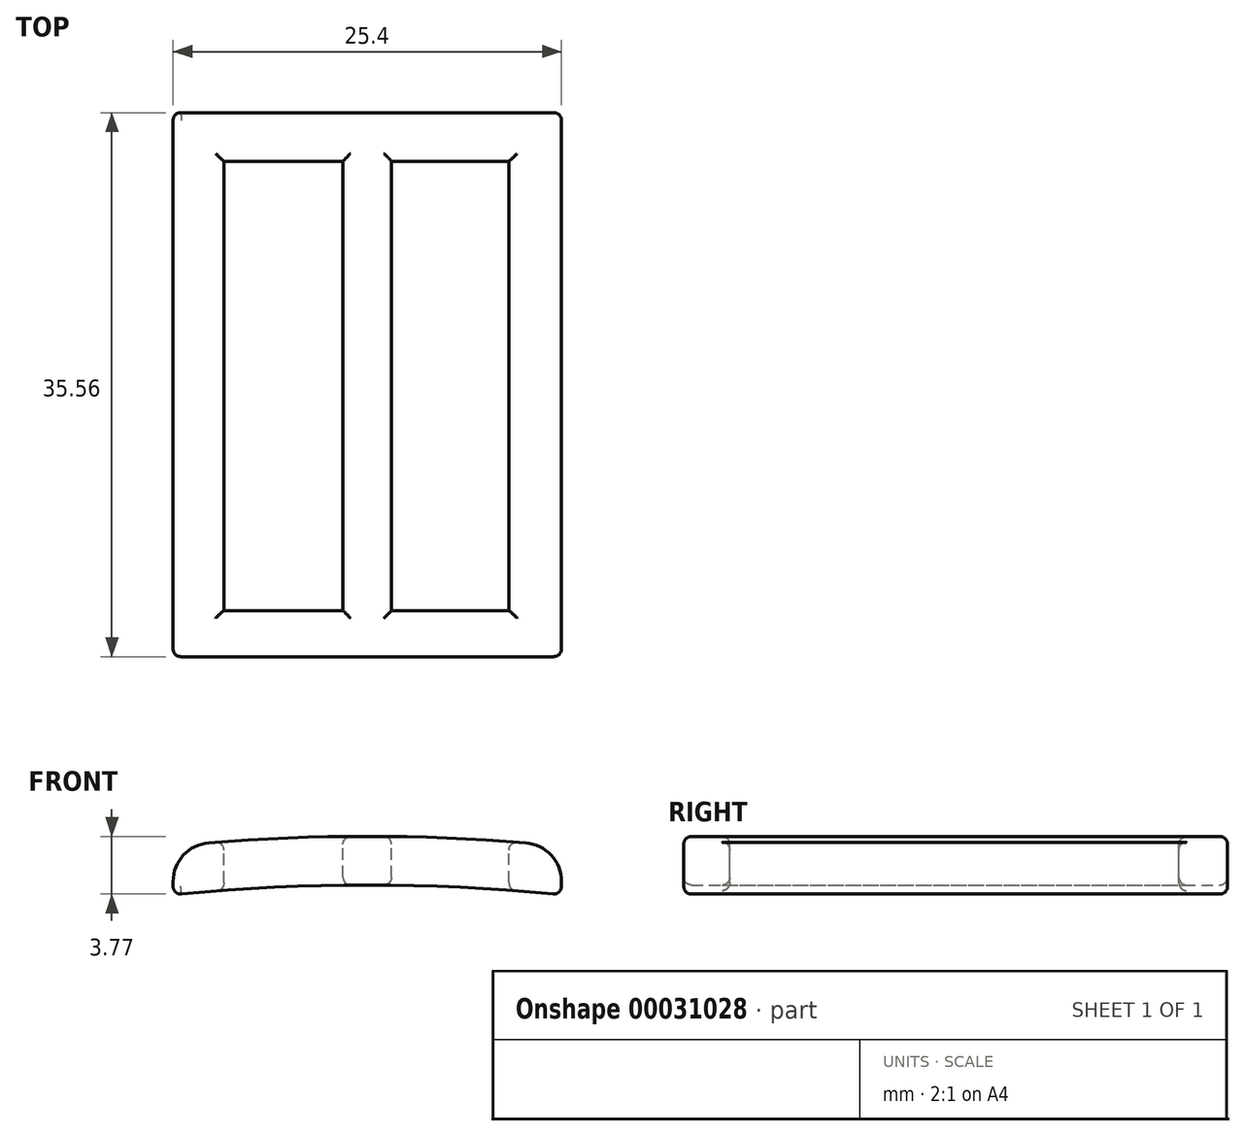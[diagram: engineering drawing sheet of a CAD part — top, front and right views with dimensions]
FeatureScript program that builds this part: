
annotation { "Feature Type Name" : "Feature", "Feature Type Description" : "" }
export const myFeature = defineFeature(function(context is Context, id is Id, definition is map)
    precondition{}
    {
        {
            var Q0;
            Q0=qCreatedBy(makeId("Front.planeOp"),FACE);
            var sketch = newSketch(context, id + "F0", { "sketchPlane" : qUnion([Q0])});
            skArc(sketch, "E0", {"start": v(10.37, 126.58) * mm, "mid": v(0, 127) * mm, "end": v(-10.37, 126.58) * mm});
            skArc(sketch, "E1", {"start": v(12.14, 123.23) * mm, "mid": v(0, 123.83) * mm, "end": v(-12.14, 123.23) * mm});
            skLineSegment(sketch, "E2", {"start": v(0, 0) * mm, "end": v(0, 187.17) * mm});
            skLineSegment(sketch, "E3", {"start": v(-12.7, 124.04) * mm, "end": v(-12.7, 123.73) * mm});
            skLineSegment(sketch, "E4", {"start": v(12.7, 124.04) * mm, "end": v(12.7, 123.73) * mm});
            skPoint(sketch, "E5.orphan", {"position": v(12.7, 106.56) * mm});
            skPoint(sketch, "E6.end.orphan", {"position": v(12.7, 140.5) * mm});
            skPoint(sketch, "E7.orphan", {"position": v(-12.7, 140.5) * mm});
            skPoint(sketch, "E8.orphan", {"position": v(-12.7, 106.56) * mm});
            skPoint(sketch, "E9.visualSharp", {"position": v(-12.7, 126.36) * mm});
            skArc(sketch, "E9.filletArc", {"start": v(-10.37, 126.58) * mm, "mid": v(-12.03, 125.77) * mm, "end": v(-12.7, 124.04) * mm});
            skPoint(sketch, "E10.visualSharp", {"position": v(-12.7, 123.17) * mm});
            skArc(sketch, "E10.filletArc", {"start": v(-12.7, 123.73) * mm, "mid": v(-12.53, 123.36) * mm, "end": v(-12.14, 123.23) * mm});
            skPoint(sketch, "E11.visualSharp", {"position": v(12.7, 126.36) * mm});
            skArc(sketch, "E11.filletArc", {"start": v(12.7, 124.04) * mm, "mid": v(12.03, 125.77) * mm, "end": v(10.37, 126.58) * mm});
            skPoint(sketch, "E12.visualSharp", {"position": v(12.7, 123.17) * mm});
            skArc(sketch, "E12.filletArc", {"start": v(12.14, 123.23) * mm, "mid": v(12.53, 123.36) * mm, "end": v(12.7, 123.73) * mm});
            skSolve(sketch);
        }
        {
            var Q0;
            Q0=makeQuery(id+"F0.imprint","IMPRINT",FACE,{"disambiguationData":[TD([[makeQuery(id+"F0.imprint","IMPRINT",EDGE,{"derivedFrom":sQuery(id+"F0.wireOp",EDGE,"E3")}),1.0]])]});
            var Q1;
            Q1=makeQuery(id+"F0.imprint","IMPRINT",FACE,{"disambiguationData":[TD([[makeQuery(id+"F0.imprint","IMPRINT",EDGE,{"derivedFrom":sQuery(id+"F0.wireOp",EDGE,"E4")}),-1.0]])]});
            extrude(context, id + "F1", {"entities" : qUnion([Q0, Q1]), "depth" : 35.56 * mm});
        }
        {
            var Q0;
            Q0=qCreatedBy(makeId("Top.planeOp"),FACE);
            cPlane(context, id + "F2", {"entities" : qUnion([Q0]), "cplaneType" : CPlaneType.OFFSET, "offset" : 127 * mm, "width" : 152.4 * mm, "height" : 152.4 * mm});
        }
        {
            var Q0;
            Q0=qCreatedBy(id+"F2.planeOp",FACE);
            var sketch = newSketch(context, id + "F3", { "sketchPlane" : qUnion([Q0])});
            skLineSegment(sketch, "E13.bottom", {"start": v(1.59, -32.55) * mm, "end": v(9.27, -32.55) * mm});
            skLineSegment(sketch, "E13.top", {"start": v(1.59, -3.18) * mm, "end": v(9.27, -3.18) * mm});
            skLineSegment(sketch, "E13.left", {"start": v(1.59, -32.55) * mm, "end": v(1.59, -3.18) * mm});
            skLineSegment(sketch, "E13.right", {"start": v(9.27, -32.55) * mm, "end": v(9.27, -3.18) * mm});
            skLineSegment(sketch, "E14.bottom", {"start": v(-1.59, -32.55) * mm, "end": v(-9.38, -32.55) * mm});
            skLineSegment(sketch, "E14.top", {"start": v(-1.59, -3.18) * mm, "end": v(-9.38, -3.18) * mm});
            skLineSegment(sketch, "E14.left", {"start": v(-1.59, -32.55) * mm, "end": v(-1.59, -3.18) * mm});
            skLineSegment(sketch, "E14.right", {"start": v(-9.38, -32.55) * mm, "end": v(-9.38, -3.18) * mm});
            skPoint(sketch, "E15.end.orphan", {"position": v(0, -32.55) * mm});
            skPoint(sketch, "E15.start.orphan", {"position": v(0, -35.72) * mm});
            skPoint(sketch, "E16.end.orphan", {"position": v(1.59, -23.43) * mm});
            skPoint(sketch, "E17.end.orphan", {"position": v(-1.59, -23.43) * mm});
            skPoint(sketch, "E18.end.orphan", {"position": v(0, -3.18) * mm});
            skSolve(sketch);
        }
        {
            var Q0;
            Q0=makeQuery(id+"F3.imprint","IMPRINT",FACE,{"disambiguationData":[TD([[makeQuery(id+"F3.imprint","IMPRINT",EDGE,{"derivedFrom":sQuery(id+"F3.wireOp",EDGE,"E13.bottom")}),1.0]])]});
            var Q1;
            Q1=makeQuery(id+"F3.imprint","IMPRINT",FACE,{"disambiguationData":[TD([[makeQuery(id+"F3.imprint","IMPRINT",EDGE,{"derivedFrom":sQuery(id+"F3.wireOp",EDGE,"E14.bottom")}),-1.0]])]});
            extrude(context, id + "F4", {"entities" : qUnion([Q0, Q1]), "operationType" : NewBodyOperationType.REMOVE, "oppositeDirection" : true, "depth" : 25.4 * mm});
        }
        {
            var Q0;
            Q0=makeQuery(id+"F1.opExtrude","CAP_EDGE",EDGE,{"disambiguationData":[OSD([sQuery(id+"F0.wireOp",EDGE,"E0")])],"isStart":false});
            var Q1;
            Q1=makeQuery(id+"F1.opExtrude","CAP_EDGE",EDGE,{"disambiguationData":[OSD([sQuery(id+"F0.wireOp",EDGE,"E0")])],"isStart":true});
            var Q2;
            Q2=makeQuery(id+"F4.boolean.opBoolean","INTERSECT",EDGE,{"derivedFrom":[makeQuery(id+"F1.opExtrude","SWEPT_FACE",FACE,{"disambiguationData":[OSD([sQuery(id+"F0.wireOp",EDGE,"E0")])]}),makeQuery(id+"F4.opExtrude","SWEPT_FACE",FACE,{"disambiguationData":[OSD([sQuery(id+"F3.wireOp",EDGE,"E13.top")])]})]});
            var Q3;
            Q3=makeQuery(id+"F4.boolean.opBoolean","INTERSECT",EDGE,{"derivedFrom":[makeQuery(id+"F1.opExtrude","SWEPT_FACE",FACE,{"disambiguationData":[OSD([sQuery(id+"F0.wireOp",EDGE,"E0")])]}),makeQuery(id+"F4.opExtrude","SWEPT_FACE",FACE,{"disambiguationData":[OSD([sQuery(id+"F3.wireOp",EDGE,"E14.top")])]})]});
            var Q4;
            Q4=makeQuery(id+"F4.boolean.opBoolean","INTERSECT",EDGE,{"derivedFrom":[makeQuery(id+"F1.opExtrude","SWEPT_FACE",FACE,{"disambiguationData":[OSD([sQuery(id+"F0.wireOp",EDGE,"E0")])]}),makeQuery(id+"F4.opExtrude","SWEPT_FACE",FACE,{"disambiguationData":[OSD([sQuery(id+"F3.wireOp",EDGE,"E14.bottom")])]})]});
            var Q5;
            Q5=makeQuery(id+"F4.boolean.opBoolean","INTERSECT",EDGE,{"derivedFrom":[makeQuery(id+"F1.opExtrude","SWEPT_FACE",FACE,{"disambiguationData":[OSD([sQuery(id+"F0.wireOp",EDGE,"E0")])]}),makeQuery(id+"F4.opExtrude","SWEPT_FACE",FACE,{"disambiguationData":[OSD([sQuery(id+"F3.wireOp",EDGE,"E13.bottom")])]})]});
            var Q6;
            Q6=makeQuery(id+"F4.boolean.opBoolean","INTERSECT",EDGE,{"derivedFrom":[makeQuery(id+"F1.opExtrude","SWEPT_FACE",FACE,{"disambiguationData":[OSD([sQuery(id+"F0.wireOp",EDGE,"E1")])]}),makeQuery(id+"F4.opExtrude","SWEPT_FACE",FACE,{"disambiguationData":[OSD([sQuery(id+"F3.wireOp",EDGE,"E13.bottom")])]})]});
            var Q7;
            Q7=makeQuery(id+"F4.boolean.opBoolean","INTERSECT",EDGE,{"derivedFrom":[makeQuery(id+"F1.opExtrude","SWEPT_FACE",FACE,{"disambiguationData":[OSD([sQuery(id+"F0.wireOp",EDGE,"E1")])]}),makeQuery(id+"F4.opExtrude","SWEPT_FACE",FACE,{"disambiguationData":[OSD([sQuery(id+"F3.wireOp",EDGE,"E14.bottom")])]})]});
            var Q8;
            Q8=makeQuery(id+"F4.boolean.opBoolean","INTERSECT",EDGE,{"derivedFrom":[makeQuery(id+"F1.opExtrude","SWEPT_FACE",FACE,{"disambiguationData":[OSD([sQuery(id+"F0.wireOp",EDGE,"E1")])]}),makeQuery(id+"F4.opExtrude","SWEPT_FACE",FACE,{"disambiguationData":[OSD([sQuery(id+"F3.wireOp",EDGE,"E13.top")])]})]});
            var Q9;
            Q9=makeQuery(id+"F4.boolean.opBoolean","INTERSECT",EDGE,{"derivedFrom":[makeQuery(id+"F1.opExtrude","SWEPT_FACE",FACE,{"disambiguationData":[OSD([sQuery(id+"F0.wireOp",EDGE,"E1")])]}),makeQuery(id+"F4.opExtrude","SWEPT_FACE",FACE,{"disambiguationData":[OSD([sQuery(id+"F3.wireOp",EDGE,"E14.top")])]})]});
            var Q10;
            Q10=makeQuery(id+"F4.boolean.opBoolean","INTERSECT",EDGE,{"derivedFrom":[makeQuery(id+"F1.opExtrude","SWEPT_FACE",FACE,{"disambiguationData":[OSD([sQuery(id+"F0.wireOp",EDGE,"E0")])]}),makeQuery(id+"F4.opExtrude","SWEPT_FACE",FACE,{"disambiguationData":[OSD([sQuery(id+"F3.wireOp",EDGE,"E14.left")])]})]});
            var Q11;
            Q11=makeQuery(id+"F4.boolean.opBoolean","INTERSECT",EDGE,{"derivedFrom":[makeQuery(id+"F1.opExtrude","SWEPT_FACE",FACE,{"disambiguationData":[OSD([sQuery(id+"F0.wireOp",EDGE,"E0")])]}),makeQuery(id+"F4.opExtrude","SWEPT_FACE",FACE,{"disambiguationData":[OSD([sQuery(id+"F3.wireOp",EDGE,"E13.left")])]})]});
            var Q12;
            Q12=makeQuery(id+"F4.boolean.opBoolean","INTERSECT",EDGE,{"derivedFrom":[makeQuery(id+"F1.opExtrude","SWEPT_FACE",FACE,{"disambiguationData":[OSD([sQuery(id+"F0.wireOp",EDGE,"E0")])]}),makeQuery(id+"F4.opExtrude","SWEPT_FACE",FACE,{"disambiguationData":[OSD([sQuery(id+"F3.wireOp",EDGE,"E13.right")])]})]});
            var Q13;
            Q13=makeQuery(id+"F4.boolean.opBoolean","INTERSECT",EDGE,{"derivedFrom":[makeQuery(id+"F1.opExtrude","SWEPT_FACE",FACE,{"disambiguationData":[OSD([sQuery(id+"F0.wireOp",EDGE,"E0")])]}),makeQuery(id+"F4.opExtrude","SWEPT_FACE",FACE,{"disambiguationData":[OSD([sQuery(id+"F3.wireOp",EDGE,"E14.right")])]})]});
            var Q14;
            Q14=makeQuery(id+"F4.boolean.opBoolean","INTERSECT",EDGE,{"derivedFrom":[makeQuery(id+"F1.opExtrude","SWEPT_FACE",FACE,{"disambiguationData":[OSD([sQuery(id+"F0.wireOp",EDGE,"E1")])]}),makeQuery(id+"F4.opExtrude","SWEPT_FACE",FACE,{"disambiguationData":[OSD([sQuery(id+"F3.wireOp",EDGE,"E14.right")])]})]});
            var Q15;
            Q15=makeQuery(id+"F4.boolean.opBoolean","INTERSECT",EDGE,{"derivedFrom":[makeQuery(id+"F1.opExtrude","SWEPT_FACE",FACE,{"disambiguationData":[OSD([sQuery(id+"F0.wireOp",EDGE,"E1")])]}),makeQuery(id+"F4.opExtrude","SWEPT_FACE",FACE,{"disambiguationData":[OSD([sQuery(id+"F3.wireOp",EDGE,"E13.left")])]})]});
            var Q16;
            Q16=makeQuery(id+"F4.boolean.opBoolean","INTERSECT",EDGE,{"derivedFrom":[makeQuery(id+"F1.opExtrude","SWEPT_FACE",FACE,{"disambiguationData":[OSD([sQuery(id+"F0.wireOp",EDGE,"E1")])]}),makeQuery(id+"F4.opExtrude","SWEPT_FACE",FACE,{"disambiguationData":[OSD([sQuery(id+"F3.wireOp",EDGE,"E14.left")])]})]});
            var Q17;
            Q17=makeQuery(id+"F4.boolean.opBoolean","INTERSECT",EDGE,{"derivedFrom":[makeQuery(id+"F1.opExtrude","SWEPT_FACE",FACE,{"disambiguationData":[OSD([sQuery(id+"F0.wireOp",EDGE,"E1")])]}),makeQuery(id+"F4.opExtrude","SWEPT_FACE",FACE,{"disambiguationData":[OSD([sQuery(id+"F3.wireOp",EDGE,"E13.right")])]})]});
            var Q18;
            Q18=makeQuery(id+"F1.opExtrude","CAP_EDGE",EDGE,{"disambiguationData":[OSD([sQuery(id+"F0.wireOp",EDGE,"E1")])],"isStart":false});
            var Q19;
            Q19=makeQuery(id+"F1.opExtrude","CAP_EDGE",EDGE,{"disambiguationData":[OSD([sQuery(id+"F0.wireOp",EDGE,"E1")])],"isStart":true});
            fillet(context, id + "F5", {"entities" : qUnion([Q0, Q1, Q2, Q3, Q4, Q5, Q6, Q7, Q8, Q9, Q10, Q11, Q12, Q13, Q14, Q15, Q16, Q17, Q18, Q19]), "radius" : 0.5 * mm, "tangentPropagation" : true, "allowEdgeOverflow" : false});
        }
    });
